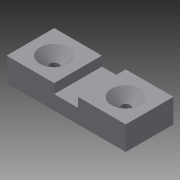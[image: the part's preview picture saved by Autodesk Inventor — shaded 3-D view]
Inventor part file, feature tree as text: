
AUTODESK INVENTOR PART (.ipt)
format: ipt  version: 2015 (Build 190159000, 159)  size: 104,960 bytes
history: native  units: mm
features: sketch x3, extrude x2, hole x1
ambient origin geometry x8: Origin, YZ Plane, XZ Plane, XY Plane, X Axis, Y Axis, Z Axis, Center Point
bodies: Solid1 (feature_tree)
feature tree (6):
  extrude  "Extrusion1"  Depth=10.0mm
  hole  "Hole1"  [1 undecoded]
  extrude  "Extrusion2"  Depth=5.0mm
  sketch  "Sketch1"  dims[d0=25.0mm d1=10.0mm]
  sketch  "Sketch2"  dims[d2=5.0mm d3=0.0mm d4=2.0mm]
  sketch  "Sketch3"  dims[d5=5.0mm d6=5.0mm d7=2.0mm d8=6.0mm d9=6.0mm d10=2.0mm d11=90.0deg d12=8.0mm d13=20.594885mm d14=10.0mm d15=10.0mm d16=2.0mm d17=0.0mm]
note: 1 required parameter value undecoded (feature->parameter linkage not recoverable at this tier; creation-order binding heuristic only, values carry confidence <= 0.55)
